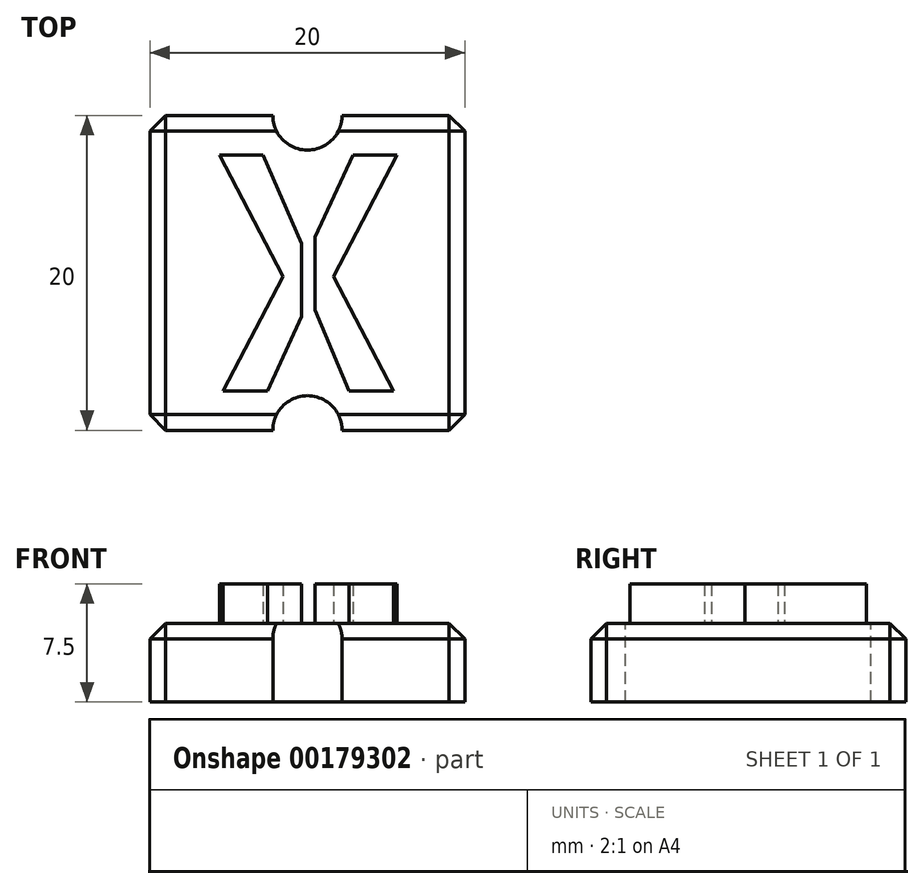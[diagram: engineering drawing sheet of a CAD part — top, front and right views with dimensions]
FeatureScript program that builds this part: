
annotation { "Feature Type Name" : "Feature", "Feature Type Description" : "" }
export const myFeature = defineFeature(function(context is Context, id is Id, definition is map)
    precondition{}
    {
        {
            var Q0;
            Q0=qCreatedBy(makeId("Top.planeOp"),FACE);
            var sketch = newSketch(context, id + "F0", { "sketchPlane" : qUnion([Q0])});
            skLineSegment(sketch, "E0.bottom", {"start": v(10, 8.66) * mm, "end": v(-10, 8.66) * mm});
            skLineSegment(sketch, "E0.top", {"start": v(10, -11.34) * mm, "end": v(-10, -11.34) * mm});
            skLineSegment(sketch, "E0.left", {"start": v(10, 8.66) * mm, "end": v(10, -11.34) * mm});
            skLineSegment(sketch, "E0.right", {"start": v(-10, 8.66) * mm, "end": v(-10, -11.34) * mm});
            skPoint(sketch, "E0.middle", {"position": v(0, -1.34) * mm});
            skArc(sketch, "E1", {"start": v(0, 12.66) * mm, "mid": v(2.83, 11.5) * mm, "end": v(4, 8.66) * mm});
            skPoint(sketch, "E1.startSnap0", {"position": v(0, 8.66) * mm});
            skArc(sketch, "E2", {"start": v(0, 12.66) * mm, "mid": v(-2.83, 11.5) * mm, "end": v(-4, 8.66) * mm});
            skArc(sketch, "E3", {"start": v(0, -15.34) * mm, "mid": v(-2.83, -14.17) * mm, "end": v(-4, -11.34) * mm});
            skPoint(sketch, "E3.startSnap0", {"position": v(0, -11.34) * mm});
            skArc(sketch, "E4", {"start": v(0, -15.34) * mm, "mid": v(2.83, -14.17) * mm, "end": v(4, -11.34) * mm});
            skSolve(sketch);
        }
        {
            var Q0;
            Q0=makeQuery(id+"F0.imprint","IMPRINT",FACE,{"disambiguationData":[TD([[makeQuery(id+"F0.imprint","IMPRINT",EDGE,{"derivedFrom":sQuery(id+"F0.wireOp",EDGE,"E0.bottom")}),1.0]])]});
            var Q1;
            {var subQ0=sQuery(id+"F0.wireOp",EDGE,"E1");Q1=makeQuery(id+"F0.imprint","IMPRINT",FACE,{"disambiguationData":[TD([[makeQuery(id+"F0.imprint","IMPRINT",EDGE,{"derivedFrom":subQ0}),-1.0]])]});}
            var Q2;
            {var subQ0=sQuery(id+"F0.wireOp",EDGE,"E3");Q2=makeQuery(id+"F0.imprint","IMPRINT",FACE,{"disambiguationData":[TD([[makeQuery(id+"F0.imprint","IMPRINT",EDGE,{"derivedFrom":subQ0}),-1.0]])]});}
            extrude(context, id + "F1", {"entities" : qUnion([Q0, Q1, Q2]), "depth" : 5 * mm});
        }
        {
            var Q0;
            Q0=makeQuery(id+"F1.opExtrude","CAP_FACE",FACE,{"disambiguationData":[OSD([sQuery(id+"F0.wireOp",EDGE,"E0.bottom"),sQuery(id+"F0.wireOp",EDGE,"E0.top"),sQuery(id+"F0.wireOp",EDGE,"E0.left"),sQuery(id+"F0.wireOp",EDGE,"E0.right")])],"isStart":false});
            var sketch = newSketch(context, id + "F2", { "sketchPlane" : qUnion([Q0])});
            skText(sketch, "E5", { "text": "X", "fontName": "AllertaStencil-Regular.ttf"});
            skLineSegment(sketch, "E6", {"start": v(-4, 8.66) * mm, "end": v(4, 8.66) * mm, "construction": true});
            skPoint(sketch, "E7", {"position": v(0, 8.66) * mm});
            skLineSegment(sketch, "E8", {"start": v(-4, -11.34) * mm, "end": v(4, -11.34) * mm, "construction": true});
            skPoint(sketch, "E9", {"position": v(0, -11.34) * mm});
            const initialGuessF2  = {"E5": [-0.0071, -0.00884, 1, 0, 0.015]};
            skSetInitialGuess(sketch, initialGuessF2);
            skSolve(sketch);
        }
        {
            var Q0;
            Q0=makeQuery(id+"F2.imprint","IMPRINT",FACE,{"disambiguationData":[TD([[makeQuery(id+"F2.imprint","IMPRINT",EDGE,{"derivedFrom":sQuery(id+"F2.wireOp",EDGE,"E5.sketch_text.stroke-7")}),-1.0]])]});
            var Q1;
            Q1=makeQuery(id+"F2.imprint","IMPRINT",FACE,{"disambiguationData":[TD([[makeQuery(id+"F2.imprint","IMPRINT",EDGE,{"derivedFrom":sQuery(id+"F2.wireOp",EDGE,"E5.sketch_text.stroke-0")}),-1.0]])]});
            extrude(context, id + "F3", {"entities" : qUnion([Q0, Q1]), "operationType" : NewBodyOperationType.ADD, "depth" : 2.5 * mm});
        }
        {
            var Q0;
            Q0=sQuery(id+"F2.wireOp",VERTEX,"E7");
            var Q1;
            Q1=makeQuery(id+"F1.opExtrude","SWEPT_BODY",BODY,{"disambiguationData":[OSD([sQuery(id+"F0.wireOp",EDGE,"E0.bottom"),sQuery(id+"F0.wireOp",EDGE,"E0.top"),sQuery(id+"F0.wireOp",EDGE,"E0.left"),sQuery(id+"F0.wireOp",EDGE,"E0.right"),sQuery(id+"F0.wireOp",EDGE,"E1"),sQuery(id+"F0.wireOp",EDGE,"E2")])]});
            hole(context, id + "F4", {"style" : HoleStyle.SIMPLE, "endStyle" : HoleEndStyle.BLIND, "standardTappedOrClearance" : lookupTablePath({ "standard" : "ISO", "fit" : "Normal", "size" : "M4", "type" : "Clearance" }), "standardBlindInLast" : lookupTablePath({ "fit" : "Standard", "standard" : "ISO", "size" : "M4", "type" : "Clearance" }), "holeDiameter" : 4.4 * mm, "holeDepth" : 25 * mm, "locations" : qUnion([Q0]), "scope" : qUnion([Q1])});
        }
        {
            var Q0;
            Q0=sQuery(id+"F2.wireOp",VERTEX,"E9");
            var Q1;
            Q1=makeQuery(id+"F1.opExtrude","SWEPT_BODY",BODY,{"disambiguationData":[OSD([sQuery(id+"F0.wireOp",EDGE,"E0.bottom"),sQuery(id+"F0.wireOp",EDGE,"E0.top"),sQuery(id+"F0.wireOp",EDGE,"E0.left"),sQuery(id+"F0.wireOp",EDGE,"E0.right"),sQuery(id+"F0.wireOp",EDGE,"E1"),sQuery(id+"F0.wireOp",EDGE,"E2"),sQuery(id+"F0.wireOp",EDGE,"E3"),sQuery(id+"F0.wireOp",EDGE,"E4")])]});
            hole(context, id + "F5", {"style" : HoleStyle.SIMPLE, "endStyle" : HoleEndStyle.BLIND, "standardTappedOrClearance" : lookupTablePath({ "standard" : "ISO", "fit" : "Normal", "size" : "M4", "type" : "Clearance" }), "standardBlindInLast" : lookupTablePath({ "fit" : "Standard", "standard" : "ISO", "size" : "M4", "type" : "Clearance" }), "holeDiameter" : 4.4 * mm, "holeDepth" : 25 * mm, "locations" : qUnion([Q0]), "scope" : qUnion([Q1])});
        }
        {
            var Q0;
            Q0=makeQuery(id+"F1.opExtrude","SWEPT_EDGE",EDGE,{"disambiguationData":[OSD([sQuery(id+"F0.wireOp",EDGE,"E0.bottom"),sQuery(id+"F0.wireOp",EDGE,"E0.left")])]});
            var Q1;
            Q1=makeQuery(id+"F1.opExtrude","SWEPT_EDGE",EDGE,{"disambiguationData":[OSD([sQuery(id+"F0.wireOp",EDGE,"E0.top"),sQuery(id+"F0.wireOp",EDGE,"E0.left")])]});
            var Q2;
            Q2=makeQuery(id+"F1.opExtrude","SWEPT_EDGE",EDGE,{"disambiguationData":[OSD([sQuery(id+"F0.wireOp",EDGE,"E0.top"),sQuery(id+"F0.wireOp",EDGE,"E0.right")])]});
            var Q3;
            Q3=makeQuery(id+"F1.opExtrude","SWEPT_EDGE",EDGE,{"disambiguationData":[OSD([sQuery(id+"F0.wireOp",EDGE,"E0.bottom"),sQuery(id+"F0.wireOp",EDGE,"E0.right")])]});
            var Q4;
            Q4=makeQuery(id+"F1.opExtrude","CAP_EDGE",EDGE,{"disambiguationData":[OSD([sQuery(id+"F0.wireOp",EDGE,"E0.left")])],"isStart":false});
            var Q5;
            Q5=makeQuery(id+"F1.opExtrude","CAP_EDGE",EDGE,{"disambiguationData":[OSD([sQuery(id+"F0.wireOp",EDGE,"E0.right")])],"isStart":false});
            var Q6;
            {var subQ0=sQuery(id+"F0.wireOp",EDGE,"E0.bottom");Q6=makeQuery(id+"F1.opExtrude","CAP_EDGE",EDGE,{"disambiguationData":[OSD([subQ0]),TDD([makeQuery(id+"F0.imprint","IMPRINT",EDGE,{"disambiguationData":[TD([[makeQuery(id+"F0.imprint","INTERSECT",VERTEX,{"derivedFrom":[subQ0,sQuery(id+"F0.wireOp",EDGE,"E0.left")]}),-1.0]])],"derivedFrom":subQ0})])],"isStart":false});}
            var Q7;
            {var subQ0=sQuery(id+"F0.wireOp",EDGE,"E0.bottom");Q7=makeQuery(id+"F1.opExtrude","CAP_EDGE",EDGE,{"disambiguationData":[OSD([subQ0]),TDD([makeQuery(id+"F0.imprint","IMPRINT",EDGE,{"disambiguationData":[TD([[makeQuery(id+"F0.imprint","INTERSECT",VERTEX,{"derivedFrom":[subQ0,sQuery(id+"F0.wireOp",EDGE,"E0.right")]}),1.0]])],"derivedFrom":subQ0})])],"isStart":false});}
            var Q8;
            {var subQ0=sQuery(id+"F0.wireOp",EDGE,"E0.top");Q8=makeQuery(id+"F1.opExtrude","CAP_EDGE",EDGE,{"disambiguationData":[OSD([subQ0]),TDD([makeQuery(id+"F0.imprint","IMPRINT",EDGE,{"disambiguationData":[TD([[makeQuery(id+"F0.imprint","INTERSECT",VERTEX,{"derivedFrom":[subQ0,sQuery(id+"F0.wireOp",EDGE,"E0.left")]}),-1.0]])],"derivedFrom":subQ0})])],"isStart":false});}
            var Q9;
            {var subQ0=sQuery(id+"F0.wireOp",EDGE,"E0.top");Q9=makeQuery(id+"F1.opExtrude","CAP_EDGE",EDGE,{"disambiguationData":[OSD([subQ0]),TDD([makeQuery(id+"F0.imprint","IMPRINT",EDGE,{"disambiguationData":[TD([[makeQuery(id+"F0.imprint","INTERSECT",VERTEX,{"derivedFrom":[subQ0,sQuery(id+"F0.wireOp",EDGE,"E0.right")]}),1.0]])],"derivedFrom":subQ0})])],"isStart":false});}
            chamfer(context, id + "F6", {"entities" : qUnion([Q0, Q1, Q2, Q3, Q4, Q5, Q6, Q7, Q8, Q9]), "width" : 1 * mm, "tangentPropagation" : true});
        }
    });
